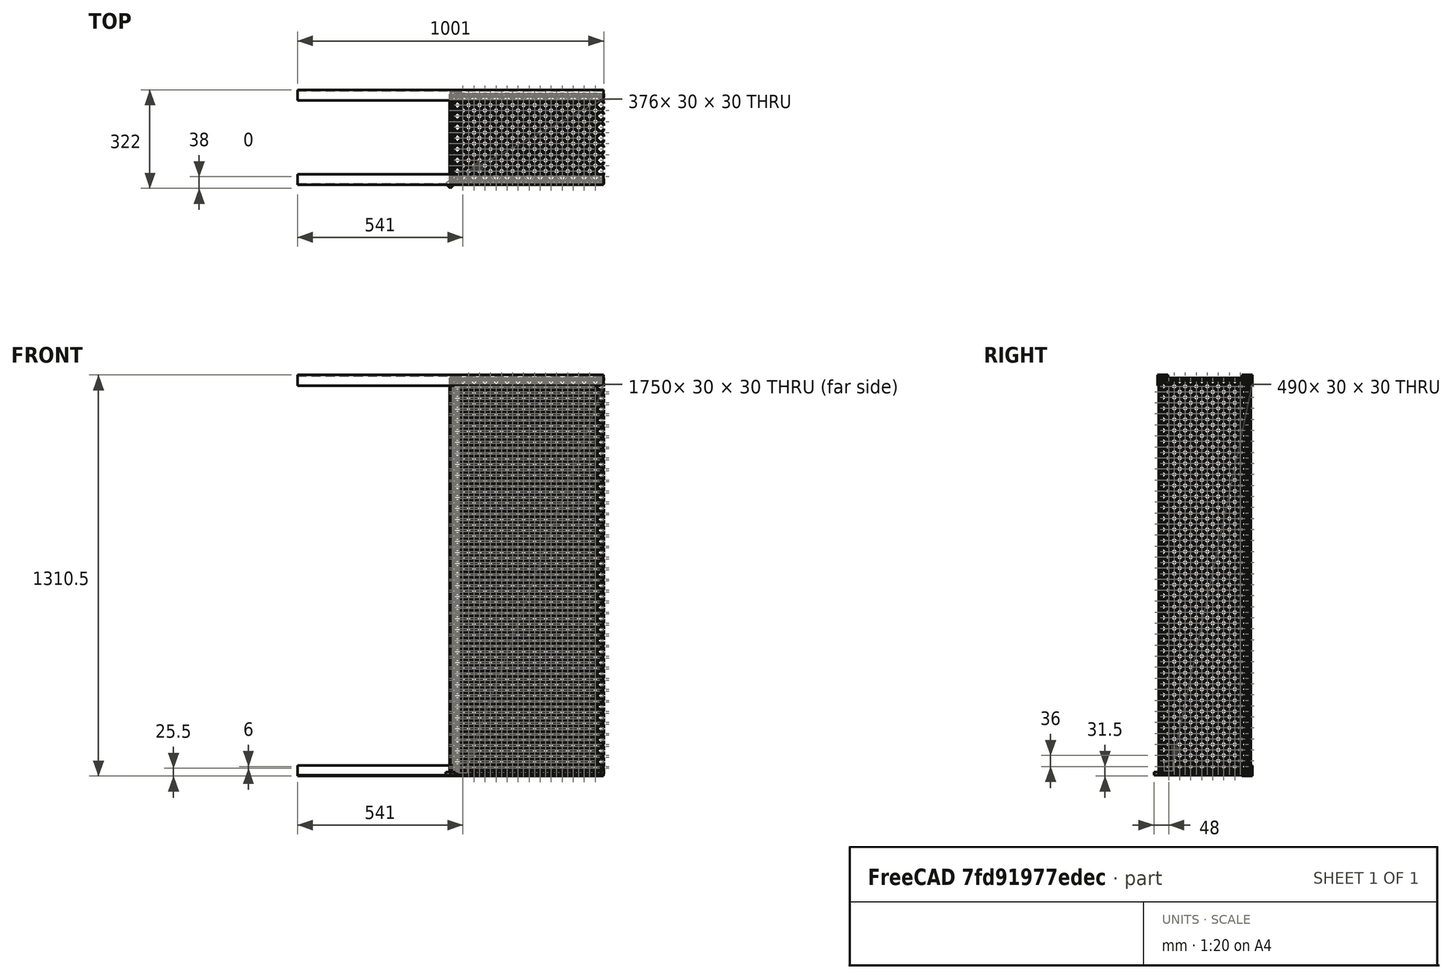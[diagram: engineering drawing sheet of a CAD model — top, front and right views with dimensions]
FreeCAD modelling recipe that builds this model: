
FCSTD DOCUMENT  (FreeCAD 0.18R16131 (Git))
Label: mechoui
License: All rights reserved
LicenseURL: http://en.wikipedia.org/wiki/All_rights_reserved
objects: PartDesign::Body×13, Part::Extrusion×10, PartDesign::FeatureBase×9, Sketcher::SketchObject×8, App::DocumentObjectGroup×8, Part::Box×5, Part::FeaturePython×5, Part::Cut×5, PartDesign::Pad×3
note: 61 computed .brp shape members not serialized (recipe doc carries the construction recipe); baked Part::Feature solids carry a one-line shape summary decoded from their .brp

FEATURE [Sketcher::SketchObject] Sketch
  MapMode = 5
  Support = -> [XY_Plane]
  sketch-geometry (6):
    g0: LineSegment StartX=35 StartY=0 StartZ=0 EndX=0 EndY=0 EndZ=0
    g1: LineSegment StartX=0 StartY=0 StartZ=0 EndX=0 EndY=35 EndZ=0
    g2: LineSegment StartX=0 StartY=35 StartZ=0 EndX=3.5 EndY=35 EndZ=0
    g3: LineSegment StartX=3.5 StartY=35 StartZ=0 EndX=3.5 EndY=3.5 EndZ=0
    g4: LineSegment StartX=3.5 StartY=3.5 StartZ=0 EndX=35 EndY=3.5 EndZ=0
    g5: LineSegment StartX=35 StartY=3.5 StartZ=0 EndX=35 EndY=0 EndZ=0
  constraints (17):
    c: PointOnObject(g0,g-1)
    c: Coincident(g0,g1)
    c: Vertical(g1)
    c: Coincident(g1,g2)
    c: Coincident(g2,g3)
    c: Vertical(g3)
    c: Coincident(g3,g4)
    c: Horizontal(g4)
    c: Coincident(g4,g5)
    c: Coincident(g5,g0)
    c: Vertical(g5)
    c: DistanceX(g0,g0) = 35
    c: DistanceY(g1,g1) = 35
    c: Horizontal(g2)
    c: DistanceY(g5,g5) = 3.5
    c: DistanceX(g2,g2) = 3.5
    c: Coincident(g0,g-1)
FEATURE [PartDesign::Pad] Pad  label="l1"
  Length = 1300
  Length2 = 100
  Profile = -> Sketch
  Type = 0
FEATURE [PartDesign::Body] Body  label="longeur1"
  Group = -> [Sketch,Pad]
  Origin = -> Origin
  Tip = -> Pad
FEATURE [PartDesign::FeatureBase] Clone  label="l2"
  BaseFeature = -> Pad
  Placement = pos=(-1.467e-13,302,1) rot=(0,0,-1;1.5708rad)
FEATURE [PartDesign::Body] Body001  label="longueur2"
  Group = -> [Clone]
  Origin = -> Origin001
  Tip = -> Clone
FEATURE [Sketcher::SketchObject] Sketch001
  AttachmentOffset = pos=(0,0,1300) rot=(-1,0,0;1.5708rad)
  MapMode = 5
  Placement = pos=(0,0,1300) rot=(-1,0,0;1.5708rad)
  Support = -> [XY_Plane002]
  sketch-geometry (6):
    g0: LineSegment StartX=35 StartY=0 StartZ=0 EndX=0 EndY=0 EndZ=0
    g1: LineSegment StartX=0 StartY=0 StartZ=0 EndX=0 EndY=35 EndZ=0
    g2: LineSegment StartX=0 StartY=35 StartZ=0 EndX=3.5 EndY=35 EndZ=0
    g3: LineSegment StartX=3.5 StartY=35 StartZ=0 EndX=3.5 EndY=3.5 EndZ=0
    g4: LineSegment StartX=3.5 StartY=3.5 StartZ=0 EndX=35 EndY=3.5 EndZ=0
    g5: LineSegment StartX=35 StartY=3.5 StartZ=0 EndX=35 EndY=0 EndZ=0
  constraints (17):
    c: PointOnObject(g0,g-1)
    c: Coincident(g0,g1)
    c: Vertical(g1)
    c: Coincident(g1,g2)
    c: Coincident(g2,g3)
    c: Vertical(g3)
    c: Coincident(g3,g4)
    c: Horizontal(g4)
    c: Coincident(g4,g5)
    c: Coincident(g5,g0)
    c: Vertical(g5)
    c: DistanceX(g0,g0) = 35
    c: DistanceY(g1,g1) = 35
    c: Horizontal(g2)
    c: DistanceY(g5,g5) = 3.5
    c: DistanceX(g2,g2) = 3.5
    c: Coincident(g0,g-1)
FEATURE [PartDesign::Pad] Pad001  label="l003"
  Length = 300
  Length2 = 100
  Profile = -> Sketch001
  Type = 0
FEATURE [PartDesign::Body] Body002  label="largeur1"
  Group = -> [Sketch001,Pad001]
  Origin = -> Origin002
  Tip = -> Pad001
FEATURE [PartDesign::FeatureBase] Clone001
  BaseFeature = -> Body002
  Placement = pos=(0,300,1300) rot=(1,0,0;3.14159rad)
FEATURE [PartDesign::Body] Body003  label="largeur2"
  Group = -> [Clone001]
  Origin = -> Origin003
  Tip = -> Clone001
FEATURE [App::DocumentObjectGroup] Group  label="Base"
  Group = -> [Body003,Body002,Body001,Body]
FEATURE [Sketcher::SketchObject] Sketch002
  AttachmentOffset = pos=(-500,-3.5,3.5) rot=(0,1,0;1.5708rad)
  MapMode = 5
  Placement = pos=(-500,-3.5,-3.5) rot=(0.57735,0.57735,0.57735;2.0944rad)
  Support = -> [XZ_Plane004]
  sketch-geometry (6):
    g0: LineSegment StartX=3.5 StartY=3.5 StartZ=0 EndX=3.5 EndY=35 EndZ=0
    g1: LineSegment StartX=3.5 StartY=35 StartZ=0 EndX=0 EndY=35 EndZ=0
    g2: LineSegment StartX=0 StartY=35 StartZ=0 EndX=0 EndY=0 EndZ=0
    g3: LineSegment StartX=0 StartY=0 StartZ=0 EndX=35 EndY=0 EndZ=0
    g4: LineSegment StartX=35 StartY=0 StartZ=0 EndX=35 EndY=3.5 EndZ=0
    g5: LineSegment StartX=35 StartY=3.5 StartZ=0 EndX=3.5 EndY=3.5 EndZ=0
  constraints (17):
    c: Vertical(g0)
    c: Coincident(g0,g1)
    c: Coincident(g1,g2)
    c: Vertical(g2)
    c: Coincident(g2,g3)
    c: Horizontal(g3)
    c: Coincident(g3,g4)
    c: Vertical(g4)
    c: Coincident(g4,g5)
    c: Coincident(g5,g0)
    c: Horizontal(g5)
    c: DistanceX(g1,g1) = 3.5
    c: Coincident(g-1,g2)
    c: DistanceY(g4,g4) = 3.5
    c: DistanceX(g3,g3) = 35
    c: DistanceY(g2,g2) = 35
    c: Horizontal(g1)
FEATURE [PartDesign::Pad] Pad002
  Length = 1000
  Length2 = 100
  Placement = pos=(0,0,0) rot=(1,0,0;1.5708rad)
  Profile = -> Sketch002
  Type = 0
FEATURE [PartDesign::Body] Body004  label="pied1"
  Group = -> [Sketch002,Pad002]
  Origin = -> Origin004
  Tip = -> Pad002
FEATURE [PartDesign::FeatureBase] Clone002
  BaseFeature = -> Body004
  Placement = pos=(0,303.5,-1.84e-14) rot=(1,0,0;1.5708rad)
FEATURE [PartDesign::Body] Body005  label="pied2"
  Group = -> [Clone002]
  Origin = -> Origin005
  Tip = -> Clone002
FEATURE [PartDesign::FeatureBase] Clone003
  BaseFeature = -> Body004
  Placement = pos=(0,5.37e-14,1303.5) rot=(1,0,0;4.71239rad)
FEATURE [PartDesign::Body] Body006  label="pied3"
  Group = -> [Clone003]
  Origin = -> Origin006
  Tip = -> Clone003
FEATURE [PartDesign::FeatureBase] Clone004
  BaseFeature = -> Body004
  Placement = pos=(0,303.5,1303.5) rot=(-1,0,0;3.14159rad)
FEATURE [PartDesign::Body] Body007  label="pied4"
  Group = -> [Clone004]
  Origin = -> Origin007
  Tip = -> Clone004
FEATURE [App::DocumentObjectGroup] Group001  label="pieds"
  Group = -> [Body004,Body005,Body006,Body007]
FEATURE [Sketcher::SketchObject] Sketch003
  MapMode = 5
  Support = -> [XY_Plane008]
  sketch-geometry (15):
    g0: LineSegment [constr] StartX=0 StartY=15 StartZ=0 EndX=0 EndY=-15 EndZ=0
    g1: LineSegment [constr] StartX=-15 StartY=0 StartZ=0 EndX=15 EndY=0 EndZ=0
    g2: LineSegment StartX=-15 StartY=0 StartZ=0 EndX=0 EndY=15 EndZ=0
    g3: LineSegment StartX=0 StartY=15 StartZ=0 EndX=15 EndY=0 EndZ=0
    g4: LineSegment StartX=15 StartY=0 StartZ=0 EndX=0 EndY=-15 EndZ=0
    g5: LineSegment StartX=0 StartY=-15 StartZ=0 EndX=-15 EndY=0 EndZ=0
    g6: LineSegment [constr] StartX=18 StartY=33 StartZ=0 EndX=18 EndY=3 EndZ=0
    g7: LineSegment [constr] StartX=3 StartY=18 StartZ=0 EndX=33 EndY=18 EndZ=0
    g8: LineSegment StartX=3 StartY=18 StartZ=0 EndX=18 EndY=33 EndZ=0
    g9: LineSegment StartX=18 StartY=33 StartZ=0 EndX=33 EndY=18 EndZ=0
    g10: LineSegment StartX=33 StartY=18 StartZ=0 EndX=18 EndY=3 EndZ=0
    g11: LineSegment StartX=18 StartY=3 StartZ=0 EndX=3 EndY=18 EndZ=0
    g12: LineSegment [constr] StartX=0 StartY=15 StartZ=0 EndX=3 EndY=18 EndZ=0
    g13: LineSegment [constr] StartX=15 StartY=0 StartZ=0 EndX=18 EndY=0 EndZ=0
    g14: LineSegment [constr] StartX=18 StartY=3 StartZ=0 EndX=18 EndY=0 EndZ=0
  constraints (36):
    c: PointOnObject(g0,g-2)
    c: PointOnObject(g1,g-1)
    c: DistanceX(g1,g1) = 30
    c: DistanceY(g0,g0) = 30
    c: Symmetric(g0,g0,g-1)
    c: Symmetric(g1,g1,g-1)
    c: Coincident(g2,g1)
    c: Coincident(g2,g0)
    c: Coincident(g3,g2)
    c: Coincident(g3,g1)
    c: Coincident(g4,g3)
    c: Coincident(g4,g0)
    c: Coincident(g5,g4)
    c: Coincident(g5,g2)
    c: Equal(g1,g7) = 30
    c: Equal(g0,g6) = 30
    c: Coincident(g8,g7)
    c: Coincident(g8,g6)
    c: Coincident(g9,g8)
    c: Coincident(g9,g7)
    c: Coincident(g10,g9)
    c: Coincident(g10,g6)
    c: Coincident(g11,g10)
    c: Coincident(g11,g8)
    c: Perpendicular(g-1,g6)
    c: Symmetric(g8,g10,g7)
    c: Symmetric(g8,g9,g6)
    c: Coincident(g12,g2)
    c: Coincident(g12,g8)
    c: Perpendicular(g12,g11)
    c: Coincident(g13,g3)
    c: PointOnObject(g13,g-1)
    c: Coincident(g14,g10)
    c: Coincident(g14,g13)
    c: Vertical(g14)
    c: DistanceX(g13,g13) = 3
FEATURE [Part::Extrusion] Extrude001
  Base = -> Sketch003
  Dir = (0,0,1)
  DirMode = 2
  FaceMakerClass = Part::FaceMakerBullseye
  LengthFwd = 10
  LengthRev = 0
  Solid = true
  Symmetric = false
FEATURE [Part::Box] Box  label="Cube"
  AttacherType = Attacher::AttachEngine3D
  Height = 10
  Length = 1290
  Placement = pos=(33,24,0) rot=(0,0,1;0rad)
  Width = 290
FEATURE [Part::Extrusion] Extrude
  Base = -> Sketch003
  Dir = (0,0,1)
  DirMode = 2
  FaceMakerClass = Part::FaceMakerBullseye
  LengthFwd = 10
  LengthRev = 0
  Solid = true
  Symmetric = false
FEATURE [Part::FeaturePython] Array  # Draft array (typed FeaturePython)
  Angle = 360
  ArrayType = 0
  Axis = (0,0,1)
  Base = -> Extrude
  Center = (0,0,0)
  Fuse = false
  IntervalAxis = (0,0,0)
  IntervalX = (36,0,0)
  IntervalY = (0,36,0)
  IntervalZ = (0,0,1)
  NumberPolar = 1
  NumberX = 38
  NumberY = 10
  NumberZ = 1
FEATURE [Part::Cut] Cut001
  Base = -> Box
  Placement = pos=(7,-21,-26) rot=(0,1,0;4.71239rad)
  Tool = -> Array
FEATURE [PartDesign::Body] Body008
  Group = -> [Sketch003]
  Origin = -> Origin008
FEATURE [App::DocumentObjectGroup] Group002  label="grille hori"
  Group = -> [Body008,Extrude001,Cut001]
FEATURE [Sketcher::SketchObject] Sketch004
  MapMode = 5
  Support = -> [XY_Plane009]
  sketch-geometry (15):
    g0: LineSegment [constr] StartX=0 StartY=15 StartZ=0 EndX=0 EndY=-15 EndZ=0
    g1: LineSegment [constr] StartX=-15 StartY=0 StartZ=0 EndX=15 EndY=0 EndZ=0
    g2: LineSegment StartX=-15 StartY=0 StartZ=0 EndX=0 EndY=15 EndZ=0
    g3: LineSegment StartX=0 StartY=15 StartZ=0 EndX=15 EndY=0 EndZ=0
    g4: LineSegment StartX=15 StartY=0 StartZ=0 EndX=0 EndY=-15 EndZ=0
    g5: LineSegment StartX=0 StartY=-15 StartZ=0 EndX=-15 EndY=0 EndZ=0
    g6: LineSegment [constr] StartX=18 StartY=33 StartZ=0 EndX=18 EndY=3 EndZ=0
    g7: LineSegment [constr] StartX=3 StartY=18 StartZ=0 EndX=33 EndY=18 EndZ=0
    g8: LineSegment StartX=3 StartY=18 StartZ=0 EndX=18 EndY=33 EndZ=0
    g9: LineSegment StartX=18 StartY=33 StartZ=0 EndX=33 EndY=18 EndZ=0
    g10: LineSegment StartX=33 StartY=18 StartZ=0 EndX=18 EndY=3 EndZ=0
    g11: LineSegment StartX=18 StartY=3 StartZ=0 EndX=3 EndY=18 EndZ=0
    g12: LineSegment [constr] StartX=0 StartY=15 StartZ=0 EndX=3 EndY=18 EndZ=0
    g13: LineSegment [constr] StartX=15 StartY=0 StartZ=0 EndX=18 EndY=0 EndZ=0
    g14: LineSegment [constr] StartX=18 StartY=3 StartZ=0 EndX=18 EndY=0 EndZ=0
  constraints (36):
    c: PointOnObject(g0,g-2)
    c: PointOnObject(g1,g-1)
    c: DistanceX(g1,g1) = 30
    c: DistanceY(g0,g0) = 30
    c: Symmetric(g0,g0,g-1)
    c: Symmetric(g1,g1,g-1)
    c: Coincident(g2,g1)
    c: Coincident(g2,g0)
    c: Coincident(g3,g2)
    c: Coincident(g3,g1)
    c: Coincident(g4,g3)
    c: Coincident(g4,g0)
    c: Coincident(g5,g4)
    c: Coincident(g5,g2)
    c: Equal(g1,g7) = 30
    c: Equal(g0,g6) = 30
    c: Coincident(g8,g7)
    c: Coincident(g8,g6)
    c: Coincident(g9,g8)
    c: Coincident(g9,g7)
    c: Coincident(g10,g9)
    c: Coincident(g10,g6)
    c: Coincident(g11,g10)
    c: Coincident(g11,g8)
    c: Perpendicular(g-1,g6)
    c: Symmetric(g8,g10,g7)
    c: Symmetric(g8,g9,g6)
    c: Coincident(g12,g2)
    c: Coincident(g12,g8)
    c: Perpendicular(g12,g11)
    c: Coincident(g13,g3)
    c: PointOnObject(g13,g-1)
    c: Coincident(g14,g10)
    c: Coincident(g14,g13)
    c: Vertical(g14)
    c: DistanceX(g13,g13) = 3
FEATURE [Part::Extrusion] Extrude002
  Base = -> Sketch004
  Dir = (0,0,1)
  DirMode = 2
  FaceMakerClass = Part::FaceMakerBullseye
  LengthFwd = 10
  LengthRev = 0
  Solid = true
  Symmetric = false
FEATURE [Part::FeaturePython] Array001  # Draft array (typed FeaturePython)
  Angle = 360
  ArrayType = 0
  Axis = (0,0,1)
  Base = -> Extrude002
  Center = (0,0,0)
  Fuse = false
  IntervalAxis = (0,0,0)
  IntervalX = (36,0,0)
  IntervalY = (0,36,0)
  IntervalZ = (0,0,1)
  NumberPolar = 1
  NumberX = 38
  NumberY = 15
  NumberZ = 1
FEATURE [Part::Extrusion] Extrude003
  Base = -> Sketch004
  Dir = (0,0,1)
  DirMode = 2
  FaceMakerClass = Part::FaceMakerBullseye
  LengthFwd = 10
  LengthRev = 0
  Solid = true
  Symmetric = false
FEATURE [Part::Box] Box001  label="Cube001"
  AttacherType = Attacher::AttachEngine3D
  Height = 10
  Length = 1290
  Placement = pos=(33,24,0) rot=(0,0,1;0rad)
  Width = 490
FEATURE [Part::Cut] Cut002
  Base = -> Box001
  Placement = pos=(-13,1,-26) rot=(0.57735,0.57735,0.57735;4.18879rad)
  Tool = -> Array001
FEATURE [PartDesign::FeatureBase] BaseFeature
  BaseFeature = -> Extrude003
FEATURE [PartDesign::Body] Body009
  BaseFeature = -> Extrude003
  Group = -> [BaseFeature,Sketch004]
  Origin = -> Origin009
  Tip = -> BaseFeature
FEATURE [App::DocumentObjectGroup] Group004  label="grille vert long 1"
  Group = -> [Body009,Extrude003,Cut002]
FEATURE [Sketcher::SketchObject] Sketch005
  MapMode = 5
  Support = -> [XY_Plane010]
  sketch-geometry (15):
    g0: LineSegment [constr] StartX=0 StartY=15 StartZ=0 EndX=0 EndY=-15 EndZ=0
    g1: LineSegment [constr] StartX=-15 StartY=0 StartZ=0 EndX=15 EndY=0 EndZ=0
    g2: LineSegment StartX=-15 StartY=0 StartZ=0 EndX=0 EndY=15 EndZ=0
    g3: LineSegment StartX=0 StartY=15 StartZ=0 EndX=15 EndY=0 EndZ=0
    g4: LineSegment StartX=15 StartY=0 StartZ=0 EndX=0 EndY=-15 EndZ=0
    g5: LineSegment StartX=0 StartY=-15 StartZ=0 EndX=-15 EndY=0 EndZ=0
    g6: LineSegment [constr] StartX=18 StartY=33 StartZ=0 EndX=18 EndY=3 EndZ=0
    g7: LineSegment [constr] StartX=3 StartY=18 StartZ=0 EndX=33 EndY=18 EndZ=0
    g8: LineSegment StartX=3 StartY=18 StartZ=0 EndX=18 EndY=33 EndZ=0
    g9: LineSegment StartX=18 StartY=33 StartZ=0 EndX=33 EndY=18 EndZ=0
    g10: LineSegment StartX=33 StartY=18 StartZ=0 EndX=18 EndY=3 EndZ=0
    g11: LineSegment StartX=18 StartY=3 StartZ=0 EndX=3 EndY=18 EndZ=0
    g12: LineSegment [constr] StartX=0 StartY=15 StartZ=0 EndX=3 EndY=18 EndZ=0
    g13: LineSegment [constr] StartX=15 StartY=0 StartZ=0 EndX=18 EndY=0 EndZ=0
    g14: LineSegment [constr] StartX=18 StartY=3 StartZ=0 EndX=18 EndY=0 EndZ=0
  constraints (36):
    c: PointOnObject(g0,g-2)
    c: PointOnObject(g1,g-1)
    c: DistanceX(g1,g1) = 30
    c: DistanceY(g0,g0) = 30
    c: Symmetric(g0,g0,g-1)
    c: Symmetric(g1,g1,g-1)
    c: Coincident(g2,g1)
    c: Coincident(g2,g0)
    c: Coincident(g3,g2)
    c: Coincident(g3,g1)
    c: Coincident(g4,g3)
    c: Coincident(g4,g0)
    c: Coincident(g5,g4)
    c: Coincident(g5,g2)
    c: Equal(g1,g7) = 30
    c: Equal(g0,g6) = 30
    c: Coincident(g8,g7)
    c: Coincident(g8,g6)
    c: Coincident(g9,g8)
    c: Coincident(g9,g7)
    c: Coincident(g10,g9)
    c: Coincident(g10,g6)
    c: Coincident(g11,g10)
    c: Coincident(g11,g8)
    c: Perpendicular(g-1,g6)
    c: Symmetric(g8,g10,g7)
    c: Symmetric(g8,g9,g6)
    c: Coincident(g12,g2)
    c: Coincident(g12,g8)
    c: Perpendicular(g12,g11)
    c: Coincident(g13,g3)
    c: PointOnObject(g13,g-1)
    c: Coincident(g14,g10)
    c: Coincident(g14,g13)
    c: Vertical(g14)
    c: DistanceX(g13,g13) = 3
FEATURE [Part::Extrusion] Extrude004
  Base = -> Sketch005
  Dir = (0,0,1)
  DirMode = 2
  FaceMakerClass = Part::FaceMakerBullseye
  LengthFwd = 10
  LengthRev = 0
  Solid = true
  Symmetric = false
FEATURE [Part::FeaturePython] Array002  # Draft array (typed FeaturePython)
  Angle = 360
  ArrayType = 0
  Axis = (0,0,1)
  Base = -> Extrude004
  Center = (0,0,0)
  Fuse = false
  IntervalAxis = (0,0,0)
  IntervalX = (36,0,0)
  IntervalY = (0,36,0)
  IntervalZ = (0,0,1)
  NumberPolar = 1
  NumberX = 38
  NumberY = 15
  NumberZ = 1
FEATURE [Part::Extrusion] Extrude005
  Base = -> Sketch005
  Dir = (0,0,1)
  DirMode = 2
  FaceMakerClass = Part::FaceMakerBullseye
  LengthFwd = 10
  LengthRev = 0
  Solid = true
  Symmetric = false
FEATURE [PartDesign::FeatureBase] BaseFeature001
  BaseFeature = -> Extrude005
FEATURE [Part::Box] Box002  label="Cube002"
  AttacherType = Attacher::AttachEngine3D
  Height = 10
  Length = 1290
  Placement = pos=(33,24,0) rot=(0,0,1;0rad)
  Width = 490
FEATURE [Part::Cut] Cut003
  Base = -> Box002
  Placement = pos=(-13,284,-32) rot=(0.57735,0.57735,0.57735;4.18879rad)
  Tool = -> Array002
FEATURE [PartDesign::Body] Body010
  BaseFeature = -> Extrude005
  Group = -> [BaseFeature001,Sketch005]
  Origin = -> Origin010
  Tip = -> BaseFeature001
FEATURE [App::DocumentObjectGroup] Group005  label="grille vert long 002"
  Group = -> [Body010,Extrude005,Cut003]
FEATURE [Sketcher::SketchObject] Sketch006
  MapMode = 5
  Support = -> [XY_Plane011]
  sketch-geometry (15):
    g0: LineSegment [constr] StartX=0 StartY=15 StartZ=0 EndX=0 EndY=-15 EndZ=0
    g1: LineSegment [constr] StartX=-15 StartY=0 StartZ=0 EndX=15 EndY=0 EndZ=0
    g2: LineSegment StartX=-15 StartY=0 StartZ=0 EndX=0 EndY=15 EndZ=0
    g3: LineSegment StartX=0 StartY=15 StartZ=0 EndX=15 EndY=0 EndZ=0
    g4: LineSegment StartX=15 StartY=0 StartZ=0 EndX=0 EndY=-15 EndZ=0
    g5: LineSegment StartX=0 StartY=-15 StartZ=0 EndX=-15 EndY=0 EndZ=0
    g6: LineSegment [constr] StartX=18 StartY=33 StartZ=0 EndX=18 EndY=3 EndZ=0
    g7: LineSegment [constr] StartX=3 StartY=18 StartZ=0 EndX=33 EndY=18 EndZ=0
    g8: LineSegment StartX=3 StartY=18 StartZ=0 EndX=18 EndY=33 EndZ=0
    g9: LineSegment StartX=18 StartY=33 StartZ=0 EndX=33 EndY=18 EndZ=0
    g10: LineSegment StartX=33 StartY=18 StartZ=0 EndX=18 EndY=3 EndZ=0
    g11: LineSegment StartX=18 StartY=3 StartZ=0 EndX=3 EndY=18 EndZ=0
    g12: LineSegment [constr] StartX=0 StartY=15 StartZ=0 EndX=3 EndY=18 EndZ=0
    g13: LineSegment [constr] StartX=15 StartY=0 StartZ=0 EndX=18 EndY=0 EndZ=0
    g14: LineSegment [constr] StartX=18 StartY=3 StartZ=0 EndX=18 EndY=0 EndZ=0
  constraints (36):
    c: PointOnObject(g0,g-2)
    c: PointOnObject(g1,g-1)
    c: DistanceX(g1,g1) = 30
    c: DistanceY(g0,g0) = 30
    c: Symmetric(g0,g0,g-1)
    c: Symmetric(g1,g1,g-1)
    c: Coincident(g2,g1)
    c: Coincident(g2,g0)
    c: Coincident(g3,g2)
    c: Coincident(g3,g1)
    c: Coincident(g4,g3)
    c: Coincident(g4,g0)
    c: Coincident(g5,g4)
    c: Coincident(g5,g2)
    c: Equal(g1,g7) = 30
    c: Equal(g0,g6) = 30
    c: Coincident(g8,g7)
    c: Coincident(g8,g6)
    c: Coincident(g9,g8)
    c: Coincident(g9,g7)
    c: Coincident(g10,g9)
    c: Coincident(g10,g6)
    c: Coincident(g11,g10)
    c: Coincident(g11,g8)
    c: Perpendicular(g-1,g6)
    c: Symmetric(g8,g10,g7)
    c: Symmetric(g8,g9,g6)
    c: Coincident(g12,g2)
    c: Coincident(g12,g8)
    c: Perpendicular(g12,g11)
    c: Coincident(g13,g3)
    c: PointOnObject(g13,g-1)
    c: Coincident(g14,g10)
    c: Coincident(g14,g13)
    c: Vertical(g14)
    c: DistanceX(g13,g13) = 3
FEATURE [Part::Extrusion] Extrude006
  Base = -> Sketch006
  Dir = (0,0,1)
  DirMode = 2
  FaceMakerClass = Part::FaceMakerBullseye
  LengthFwd = 10
  LengthRev = 0
  Solid = true
  Symmetric = false
FEATURE [Part::FeaturePython] Array003  # Draft array (typed FeaturePython)
  Angle = 360
  ArrayType = 0
  Axis = (0,0,1)
  Base = -> Extrude006
  Center = (0,0,0)
  Fuse = false
  IntervalAxis = (0,0,0)
  IntervalX = (36,0,0)
  IntervalY = (0,36,0)
  IntervalZ = (0,0,1)
  NumberPolar = 1
  NumberX = 38
  NumberY = 15
  NumberZ = 1
FEATURE [Part::Extrusion] Extrude007
  Base = -> Sketch006
  Dir = (0,0,1)
  DirMode = 2
  FaceMakerClass = Part::FaceMakerBullseye
  LengthFwd = 10
  LengthRev = 0
  Solid = true
  Symmetric = false
FEATURE [PartDesign::FeatureBase] BaseFeature002
  BaseFeature = -> Extrude007
FEATURE [Part::Box] Box003  label="Cube003"
  AttacherType = Attacher::AttachEngine3D
  Height = 10
  Length = 290
  Placement = pos=(33,24,0) rot=(0,0,1;0rad)
  Width = 490
FEATURE [Part::Cut] Cut004
  Base = -> Box003
  Placement = pos=(-13,329,3) rot=(0,0,1;4.71239rad)
  Tool = -> Array003
FEATURE [PartDesign::Body] Body011
  BaseFeature = -> Extrude007
  Group = -> [BaseFeature002,Sketch006]
  Origin = -> Origin011
  Tip = -> BaseFeature002
FEATURE [App::DocumentObjectGroup] Group006  label="grille vert larg 1"
  Group = -> [Body011,Extrude007,Cut004]
FEATURE [Sketcher::SketchObject] Sketch007
  MapMode = 5
  Support = -> [XY_Plane012]
  sketch-geometry (15):
    g0: LineSegment [constr] StartX=0 StartY=15 StartZ=0 EndX=0 EndY=-15 EndZ=0
    g1: LineSegment [constr] StartX=-15 StartY=0 StartZ=0 EndX=15 EndY=0 EndZ=0
    g2: LineSegment StartX=-15 StartY=0 StartZ=0 EndX=0 EndY=15 EndZ=0
    g3: LineSegment StartX=0 StartY=15 StartZ=0 EndX=15 EndY=0 EndZ=0
    g4: LineSegment StartX=15 StartY=0 StartZ=0 EndX=0 EndY=-15 EndZ=0
    g5: LineSegment StartX=0 StartY=-15 StartZ=0 EndX=-15 EndY=0 EndZ=0
    g6: LineSegment [constr] StartX=18 StartY=33 StartZ=0 EndX=18 EndY=3 EndZ=0
    g7: LineSegment [constr] StartX=3 StartY=18 StartZ=0 EndX=33 EndY=18 EndZ=0
    g8: LineSegment StartX=3 StartY=18 StartZ=0 EndX=18 EndY=33 EndZ=0
    g9: LineSegment StartX=18 StartY=33 StartZ=0 EndX=33 EndY=18 EndZ=0
    g10: LineSegment StartX=33 StartY=18 StartZ=0 EndX=18 EndY=3 EndZ=0
    g11: LineSegment StartX=18 StartY=3 StartZ=0 EndX=3 EndY=18 EndZ=0
    g12: LineSegment [constr] StartX=0 StartY=15 StartZ=0 EndX=3 EndY=18 EndZ=0
    g13: LineSegment [constr] StartX=15 StartY=0 StartZ=0 EndX=18 EndY=0 EndZ=0
    g14: LineSegment [constr] StartX=18 StartY=3 StartZ=0 EndX=18 EndY=0 EndZ=0
  constraints (36):
    c: PointOnObject(g0,g-2)
    c: PointOnObject(g1,g-1)
    c: DistanceX(g1,g1) = 30
    c: DistanceY(g0,g0) = 30
    c: Symmetric(g0,g0,g-1)
    c: Symmetric(g1,g1,g-1)
    c: Coincident(g2,g1)
    c: Coincident(g2,g0)
    c: Coincident(g3,g2)
    c: Coincident(g3,g1)
    c: Coincident(g4,g3)
    c: Coincident(g4,g0)
    c: Coincident(g5,g4)
    c: Coincident(g5,g2)
    c: Equal(g1,g7) = 30
    c: Equal(g0,g6) = 30
    c: Coincident(g8,g7)
    c: Coincident(g8,g6)
    c: Coincident(g9,g8)
    c: Coincident(g9,g7)
    c: Coincident(g10,g9)
    c: Coincident(g10,g6)
    c: Coincident(g11,g10)
    c: Coincident(g11,g8)
    c: Perpendicular(g-1,g6)
    c: Symmetric(g8,g10,g7)
    c: Symmetric(g8,g9,g6)
    c: Coincident(g12,g2)
    c: Coincident(g12,g8)
    c: Perpendicular(g12,g11)
    c: Coincident(g13,g3)
    c: PointOnObject(g13,g-1)
    c: Coincident(g14,g10)
    c: Coincident(g14,g13)
    c: Vertical(g14)
    c: DistanceX(g13,g13) = 3
FEATURE [Part::Extrusion] Extrude008
  Base = -> Sketch007
  Dir = (0,0,1)
  DirMode = 2
  FaceMakerClass = Part::FaceMakerBullseye
  LengthFwd = 10
  LengthRev = 0
  Solid = true
  Symmetric = false
FEATURE [Part::FeaturePython] Array004  # Draft array (typed FeaturePython)
  Angle = 360
  ArrayType = 0
  Axis = (0,0,1)
  Base = -> Extrude008
  Center = (0,0,0)
  Fuse = false
  IntervalAxis = (0,0,0)
  IntervalX = (36,0,0)
  IntervalY = (0,36,0)
  IntervalZ = (0,0,1)
  NumberPolar = 1
  NumberX = 38
  NumberY = 15
  NumberZ = 1
FEATURE [Part::Box] Box004  label="Cube004"
  AttacherType = Attacher::AttachEngine3D
  Height = 10
  Length = 290
  Placement = pos=(33,24,0) rot=(0,0,1;0rad)
  Width = 490
FEATURE [Part::Extrusion] Extrude009
  Base = -> Sketch007
  Dir = (0,0,1)
  DirMode = 2
  FaceMakerClass = Part::FaceMakerBullseye
  LengthFwd = 10
  LengthRev = 0
  Solid = true
  Symmetric = false
FEATURE [PartDesign::FeatureBase] BaseFeature003
  BaseFeature = -> Extrude009
FEATURE [Part::Cut] Cut005
  Base = -> Box004
  Placement = pos=(-13,329,1288) rot=(0,0,-1;1.5708rad)
  Tool = -> Array004
FEATURE [PartDesign::Body] Body012
  BaseFeature = -> Extrude009
  Group = -> [BaseFeature003,Sketch007]
  Origin = -> Origin012
  Tip = -> BaseFeature003
FEATURE [App::DocumentObjectGroup] Group007  label="grille vert larg 002"
  Group = -> [Body012,Extrude009,Cut005]
FEATURE [App::DocumentObjectGroup] Group003  label="grilles"
  Group = -> [Group002,Group004,Group005,Group006,Group007]
